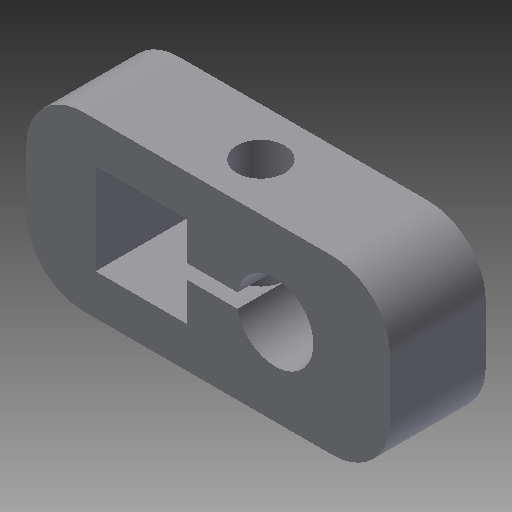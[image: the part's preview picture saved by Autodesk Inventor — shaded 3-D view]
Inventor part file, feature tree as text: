
AUTODESK INVENTOR PART (.ipt)
format: ipt  version: 2017 SP1 (Build 210196100, 196)  size: 144,896 bytes
history: native  units: mm
features: extrude x4, sketch x3, fillet x1, projected_geometry x1
ambient origin geometry x8: Origin, YZ Plane, XZ Plane, XY Plane, X Axis, Y Axis, Z Axis, Center Point
bodies: Solid1 (feature_tree)
feature tree (9):
  extrude  "Extrusion1"  Depth=14.0mm
  extrude  "Extrusion2"  Depth=18.0mm
  fillet  "Fillet1"  Radius=10.0mm
  extrude  "Extrusion3"  Depth=10.0mm TaperAngle=0.0deg
  extrude  "Extrusion4"  Depth=6.0mm
  sketch  "Sketch1"  dims[d0=8.0mm d1=14.0mm]
  sketch  "Sketch3"  dims[d2=12.0mm d3=18.0mm d4=10.0mm d5=0.0mm]
  sketch  "Sketch4"  dims[d6=5.0mm d7=8.0mm d8=0.0mm d9=6.0mm d10=1.5mm d11=8.0mm d12=0.0mm d13=38.0mm d14=9.525mm d15=10.0mm d16=0.0mm d17=19.5mm]
  projected_geometry  "Projected Loop1"
